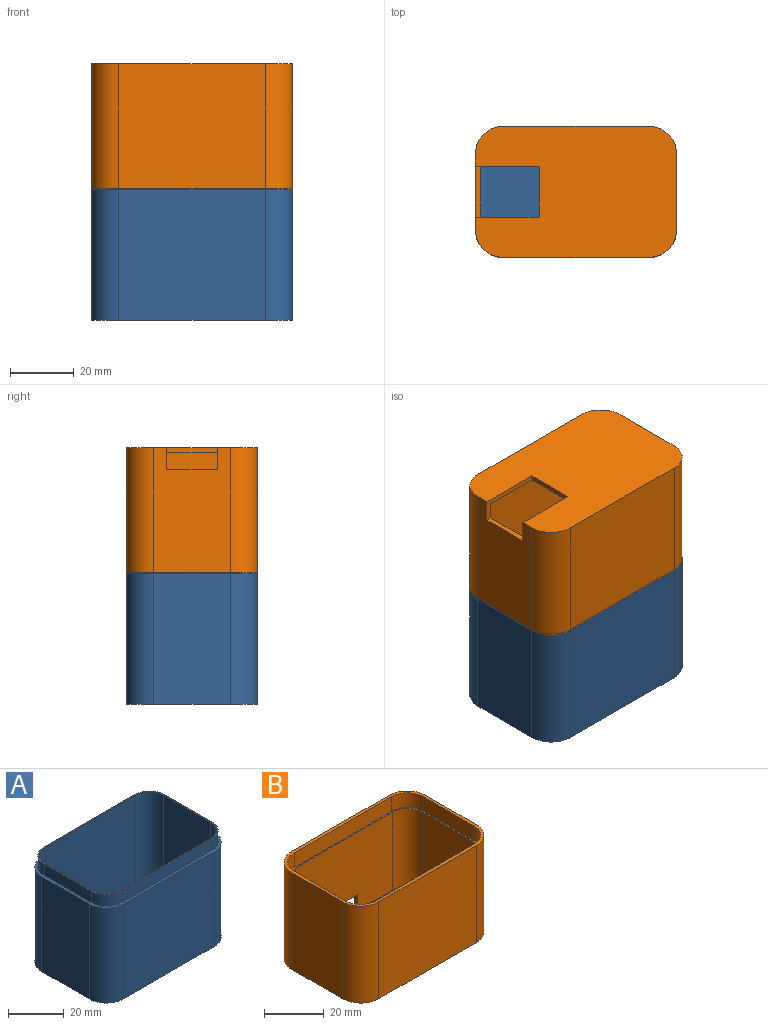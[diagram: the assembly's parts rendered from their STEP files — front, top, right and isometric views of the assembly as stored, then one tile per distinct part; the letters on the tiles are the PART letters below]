
ASSEMBLY  parts=2 mates=1
PART A: 28 faces, bbox 63.2x41.2x46.6 mm
  f0: plane 63.2x41.2mm, normal (0,0,1), area 209.6mm2, adj f1,f2,f3,f4,f5,f6,f7,f8
  f1: plane 46x41.6mm, normal (0,1,0), area 1913.6mm2, adj f0,f2,f8,f9
  f2: cylinder r=8.6mm len=41.6mm, axis (0,0,-1), area 562mm2, adj f0,f1,f3,f9
  f3: plane 41.6x24mm, normal (-1,0,0), area 998.4mm2, adj f0,f2,f4,f9
  f4: cylinder r=8.6mm len=41.6mm, axis (0,0,-1), area 562mm2, adj f0,f3,f5,f9
  f5: plane 46x41.6mm, normal (0,-1,0), area 1913.6mm2, adj f0,f4,f6,f9
  f6: cylinder r=8.6mm len=41.6mm, axis (0,0,-1), area 562mm2, adj f0,f5,f7,f9
  f7: plane 41.6x24mm, normal (1,0,0), area 998.4mm2, adj f0,f6,f8,f9
  f8: cylinder r=8.6mm len=41.6mm, axis (0,0,-1), area 562mm2, adj f0,f1,f7,f9
  f9: plane 63.2x41.2mm, normal (0,0,-1), area 2540.4mm2, adj f1,f2,f3,f4,f5,f6,f7,f8
  f10: cylinder r=7.5mm len=7.5mm, axis (0,0,-1), area 58.9mm2, adj f0,f11,f17,f18
  f11: plane 24x5mm, normal (1,0,0), area 120mm2, adj f0,f10,f12,f18
  f12: cylinder r=7.5mm len=7.5mm, axis (0,0,-1), area 58.9mm2, adj f0,f11,f13,f18
  f13: plane 46x5mm, normal (0,1,0), area 230mm2, adj f0,f12,f14,f18
  f14: cylinder r=7.5mm len=7.5mm, axis (0,0,-1), area 58.9mm2, adj f0,f13,f15,f18
  f15: plane 24x5mm, normal (-1,0,0), area 120mm2, adj f0,f14,f16,f18
  f16: cylinder r=7.5mm len=7.5mm, axis (0,0,-1), area 58.9mm2, adj f0,f15,f17,f18
  f17: plane 46x5mm, normal (0,-1,0), area 230mm2, adj f0,f10,f16,f18
  f18: plane 61x39mm, normal (0,0,1), area 92.8mm2, adj f10,f11,f12,f13,f14,f15,f16,f17
  f19: plane 60x38mm, normal (0,0,1), area 2237.9mm2, adj f20,f21,f22,f23,f24,f25,f26,f27
  f20: plane 45x24mm, normal (1,0,0), area 1080mm2, adj f18,f19,f21,f27
  f21: cylinder r=7mm len=45mm, axis (0,0,-1), area 494.8mm2, adj f18,f19,f20,f22
  f22: plane 46x45mm, normal (0,1,0), area 2070mm2, adj f18,f19,f21,f23
  f23: cylinder r=7mm len=45mm, axis (0,0,-1), area 494.8mm2, adj f18,f19,f22,f24
  f24: plane 45x24mm, normal (-1,0,0), area 1080mm2, adj f18,f19,f23,f25
  f25: cylinder r=7mm len=45mm, axis (0,0,-1), area 494.8mm2, adj f18,f19,f24,f26
  f26: plane 46x45mm, normal (0,-1,0), area 2070mm2, adj f18,f19,f25,f27
  f27: cylinder r=7mm len=45mm, axis (0,0,-1), area 494.8mm2, adj f18,f19,f20,f26
PART B: 36 faces, bbox 63.2x41.2x39.6 mm
  f0: plane 60x38mm, normal (0,0,1), area 1943.5mm2, adj f1,f21,f22,f23,f24,f25,f26,f27
  f1: plane 32x24mm, normal (-1,0,0), area 681.6mm2, adj f0,f20,f21,f27,f32,f33,f35
  f2: plane 39.6x24mm, normal (1,0,0), area 838.4mm2, adj f3,f9,f10,f11,f32,f33,f35
  f3: cylinder r=8.6mm len=39.6mm, axis (0,0,-1), area 535mm2, adj f2,f4,f10,f11
  f4: plane 46x39.6mm, normal (0,1,0), area 1743.6mm2, adj f3,f5,f10,f11,f28,f29,f30,f31
  f5: cylinder r=8.6mm len=39.6mm, axis (0,0,-1), area 535mm2, adj f4,f6,f10,f11
  f6: plane 39.6x24mm, normal (-1,0,0), area 950.4mm2, adj f5,f7,f10,f11
  f7: cylinder r=8.6mm len=39.6mm, axis (0,0,-1), area 535mm2, adj f6,f8,f10,f11
  f8: plane 46x39.6mm, normal (0,-1,0), area 1821.6mm2, adj f7,f9,f10,f11
  f9: cylinder r=8.6mm len=39.6mm, axis (0,0,-1), area 535mm2, adj f2,f8,f10,f11
  f10: plane 63.2x41.2mm, normal (0,0,1), area 209.6mm2, adj f2,f3,f4,f5,f6,f7,f8,f9
  f11: plane 63.2x41.2mm, normal (0,0,-1), area 2220.4mm2, adj f2,f3,f4,f5,f6,f7,f8,f9
  f12: cylinder r=7.5mm len=7.5mm, axis (0,0,1), area 70.7mm2, adj f10,f13,f19,f20
  f13: plane 24x6mm, normal (-1,0,0), area 144mm2, adj f10,f12,f14,f20
  f14: cylinder r=7.5mm len=7.5mm, axis (0,0,1), area 70.7mm2, adj f10,f13,f15,f20
  f15: plane 46x6mm, normal (0,-1,0), area 276mm2, adj f10,f14,f16,f20
  f16: cylinder r=7.5mm len=7.5mm, axis (0,0,1), area 70.7mm2, adj f10,f15,f17,f20
  f17: plane 24x6mm, normal (1,0,0), area 144mm2, adj f10,f16,f18,f20
  f18: cylinder r=7.5mm len=7.5mm, axis (0,0,1), area 70.7mm2, adj f10,f17,f19,f20
  f19: plane 46x6mm, normal (0,1,0), area 276mm2, adj f10,f12,f18,f20
  f20: plane 61x39mm, normal (0,0,1), area 92.8mm2, adj f1,f12,f13,f14,f15,f16,f17,f18
  f21: cylinder r=7mm len=32mm, axis (0,0,-1), area 351.9mm2, adj f0,f1,f20,f22
  f22: plane 46x32mm, normal (0,1,0), area 1472mm2, adj f0,f20,f21,f23
  f23: cylinder r=7mm len=32mm, axis (0,0,-1), area 351.9mm2, adj f0,f20,f22,f24
  f24: plane 32x24mm, normal (1,0,0), area 768mm2, adj f0,f20,f23,f25
  f25: cylinder r=7mm len=32mm, axis (0,0,-1), area 351.9mm2, adj f0,f20,f24,f26
  f26: plane 46x32mm, normal (0,-1,0), area 1394mm2, adj f0,f20,f25,f27,f28,f29,f30,f31
  f27: cylinder r=7mm len=32mm, axis (0,0,-1), area 351.9mm2, adj f0,f1,f20,f26
  f28: plane 6x1.6mm, normal (1,0,0), area 9.6mm2, adj f4,f26,f29,f31
  f29: plane 13x1.6mm, normal (0,0,-1), area 20.8mm2, adj f4,f26,f28,f30
  f30: plane 6x1.6mm, normal (-1,0,0), area 9.6mm2, adj f4,f26,f29,f31
  f31: plane 13x1.6mm, normal (0,0,1), area 20.8mm2, adj f4,f26,f28,f30
  f32: plane 20x7mm, normal (0,-1,0), area 40.6mm2, adj f0,f1,f2,f11,f34,f35
  f33: plane 20x7mm, normal (0,1,0), area 40.6mm2, adj f0,f1,f2,f11,f34,f35
  f34: plane 16x1.6mm, normal (1,0,0), area 25.6mm2, adj f0,f11,f32,f33
  f35: plane 16x1.6mm, normal (0,0,-1), area 25.6mm2, adj f1,f2,f32,f33
PLACE A t=(-59.74,0.94,-1.6)mm
PLACE B rot(axis=(0,-1,0),180deg) t=(-68.5,-57.6,75.9)mm
MATE fastened A.f13 <-> B.f15  axis (0,1,0) through (-61.45,16.95,40.9)mm
